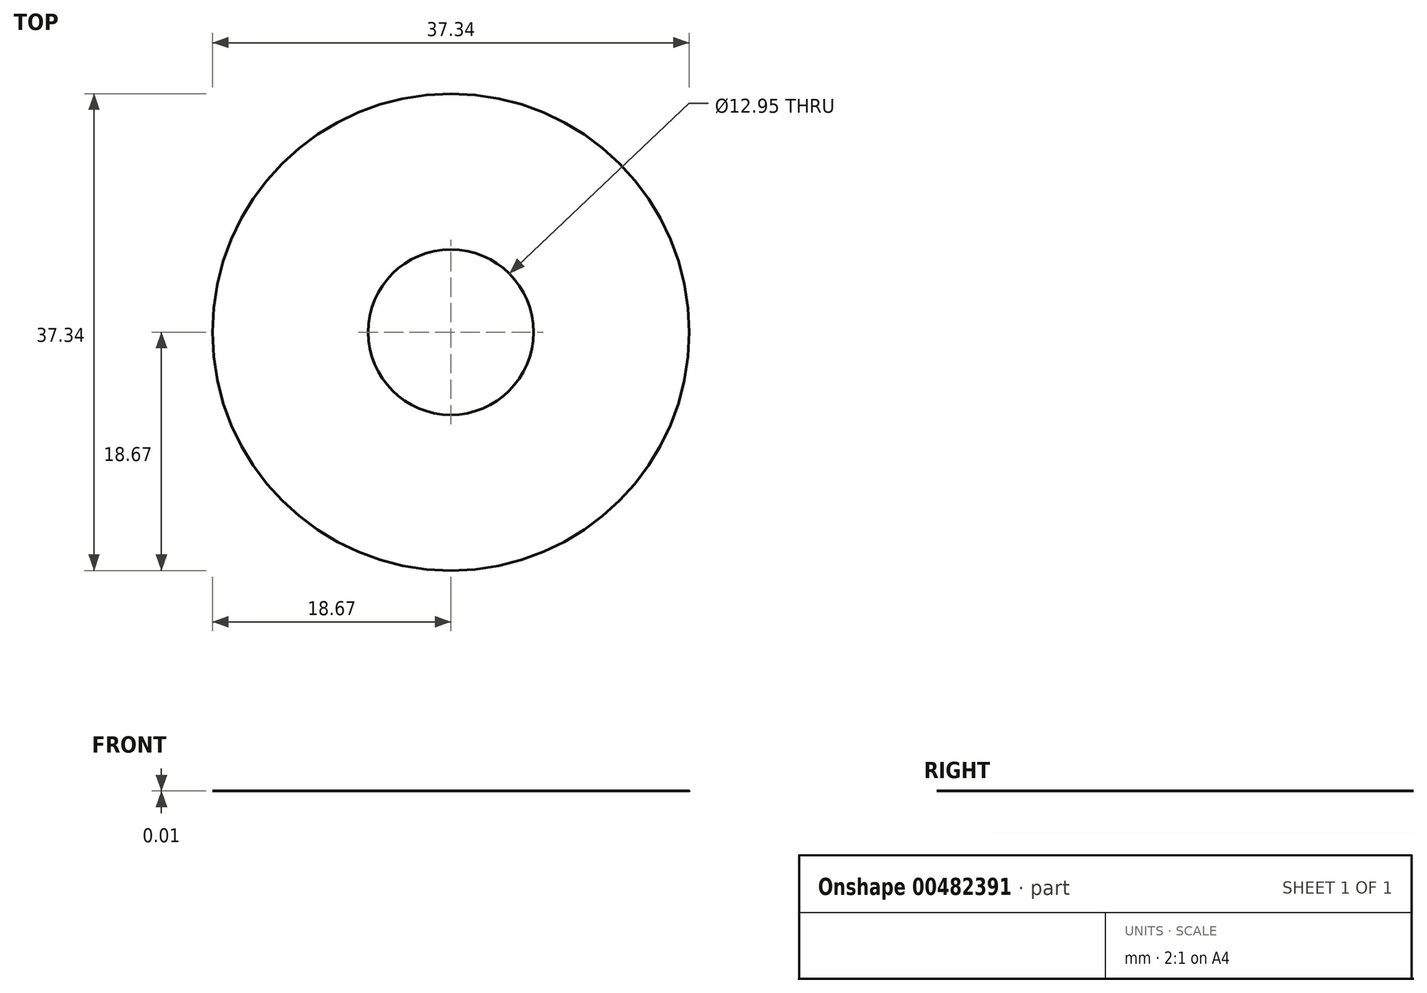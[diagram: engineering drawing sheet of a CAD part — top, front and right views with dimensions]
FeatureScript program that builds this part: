
annotation { "Feature Type Name" : "Feature", "Feature Type Description" : "" }
export const myFeature = defineFeature(function(context is Context, id is Id, definition is map)
    precondition{}
    {
        {
            var Q0;
            Q0=qCreatedBy(makeId("Top.planeOp"),FACE);
            var sketch = newSketch(context, id + "F0", { "sketchPlane" : qUnion([Q0])});
            skCircle(sketch, "E0", {"center": v(0, 0) * mm, "radius": 18.67 * mm});
            skCircle(sketch, "E1.cCircle", {"center": v(0, 0) * mm, "radius": 6.48 * mm, "construction": true});
            skLineSegment(sketch, "E1.0", {"start": v(-3.74, 6.48) * mm, "end": v(3.74, 6.48) * mm});
            skLineSegment(sketch, "E1.1", {"start": v(3.74, 6.48) * mm, "end": v(7.48, 0) * mm});
            skLineSegment(sketch, "E1.2", {"start": v(7.48, 0) * mm, "end": v(3.74, -6.48) * mm});
            skLineSegment(sketch, "E1.3", {"start": v(3.74, -6.48) * mm, "end": v(-3.74, -6.48) * mm});
            skLineSegment(sketch, "E1.4", {"start": v(-3.74, -6.48) * mm, "end": v(-7.48, 0) * mm});
            skLineSegment(sketch, "E1.5", {"start": v(-7.48, 0) * mm, "end": v(-3.74, 6.48) * mm});
            skPoint(sketch, "E1.0.midPoint", {"position": v(0, 6.48) * mm});
            skCircle(sketch, "E2", {"center": v(0, 0) * mm, "radius": 6.48 * mm});
            skSolve(sketch);
        }
        {
            var Q0;
            Q0 = qSketchRegion(id + "F0", true);
            var Q1;
            Q1=makeQuery(id+"F0.imprint","IMPRINT",FACE,{"disambiguationData":[TD([[makeQuery(id+"F0.imprint","IMPRINT",EDGE,{"derivedFrom":sQuery(id+"F0.wireOp",EDGE,"E1.0")}),-1.0]])]});
            var Q2;
            {var subQ0=sQuery(id+"F0.wireOp",EDGE,"E1.3");var subQ1=sQuery(id+"F0.wireOp",EDGE,"E1.2");var subQ2=makeQuery(id+"F0.imprint","INTERSECT",VERTEX,{"derivedFrom":[subQ1,subQ0]});Q2=makeQuery(id+"F0.imprint","IMPRINT",FACE,{"disambiguationData":[TD([[makeQuery(id+"F0.imprint","IMPRINT",EDGE,{"disambiguationData":[TD([[subQ2,1.0]])],"derivedFrom":subQ1}),-1.0]])]});}
            var Q3;
            {var subQ0=sQuery(id+"F0.wireOp",EDGE,"E1.2");var subQ1=sQuery(id+"F0.wireOp",EDGE,"E1.1");var subQ2=makeQuery(id+"F0.imprint","INTERSECT",VERTEX,{"derivedFrom":[subQ1,subQ0]});Q3=makeQuery(id+"F0.imprint","IMPRINT",FACE,{"disambiguationData":[TD([[makeQuery(id+"F0.imprint","IMPRINT",EDGE,{"disambiguationData":[TD([[subQ2,1.0]])],"derivedFrom":subQ1}),-1.0]])]});}
            var Q4;
            {var subQ0=sQuery(id+"F0.wireOp",EDGE,"E1.4");var subQ1=sQuery(id+"F0.wireOp",EDGE,"E1.3");var subQ2=makeQuery(id+"F0.imprint","INTERSECT",VERTEX,{"derivedFrom":[subQ1,subQ0]});Q4=makeQuery(id+"F0.imprint","IMPRINT",FACE,{"disambiguationData":[TD([[makeQuery(id+"F0.imprint","IMPRINT",EDGE,{"disambiguationData":[TD([[subQ2,1.0]])],"derivedFrom":subQ1}),-1.0]])]});}
            var Q5;
            {var subQ0=sQuery(id+"F0.wireOp",EDGE,"E1.5");var subQ1=sQuery(id+"F0.wireOp",EDGE,"E1.4");var subQ2=makeQuery(id+"F0.imprint","INTERSECT",VERTEX,{"derivedFrom":[subQ1,subQ0]});Q5=makeQuery(id+"F0.imprint","IMPRINT",FACE,{"disambiguationData":[TD([[makeQuery(id+"F0.imprint","IMPRINT",EDGE,{"disambiguationData":[TD([[subQ2,1.0]])],"derivedFrom":subQ1}),-1.0]])]});}
            extrude(context, id + "F1", {"entities" : qUnion([Q0, Q1, Q2, Q3, Q4, Q5]), "depth" : .26 / 50.8 * mm});
        }
    });
